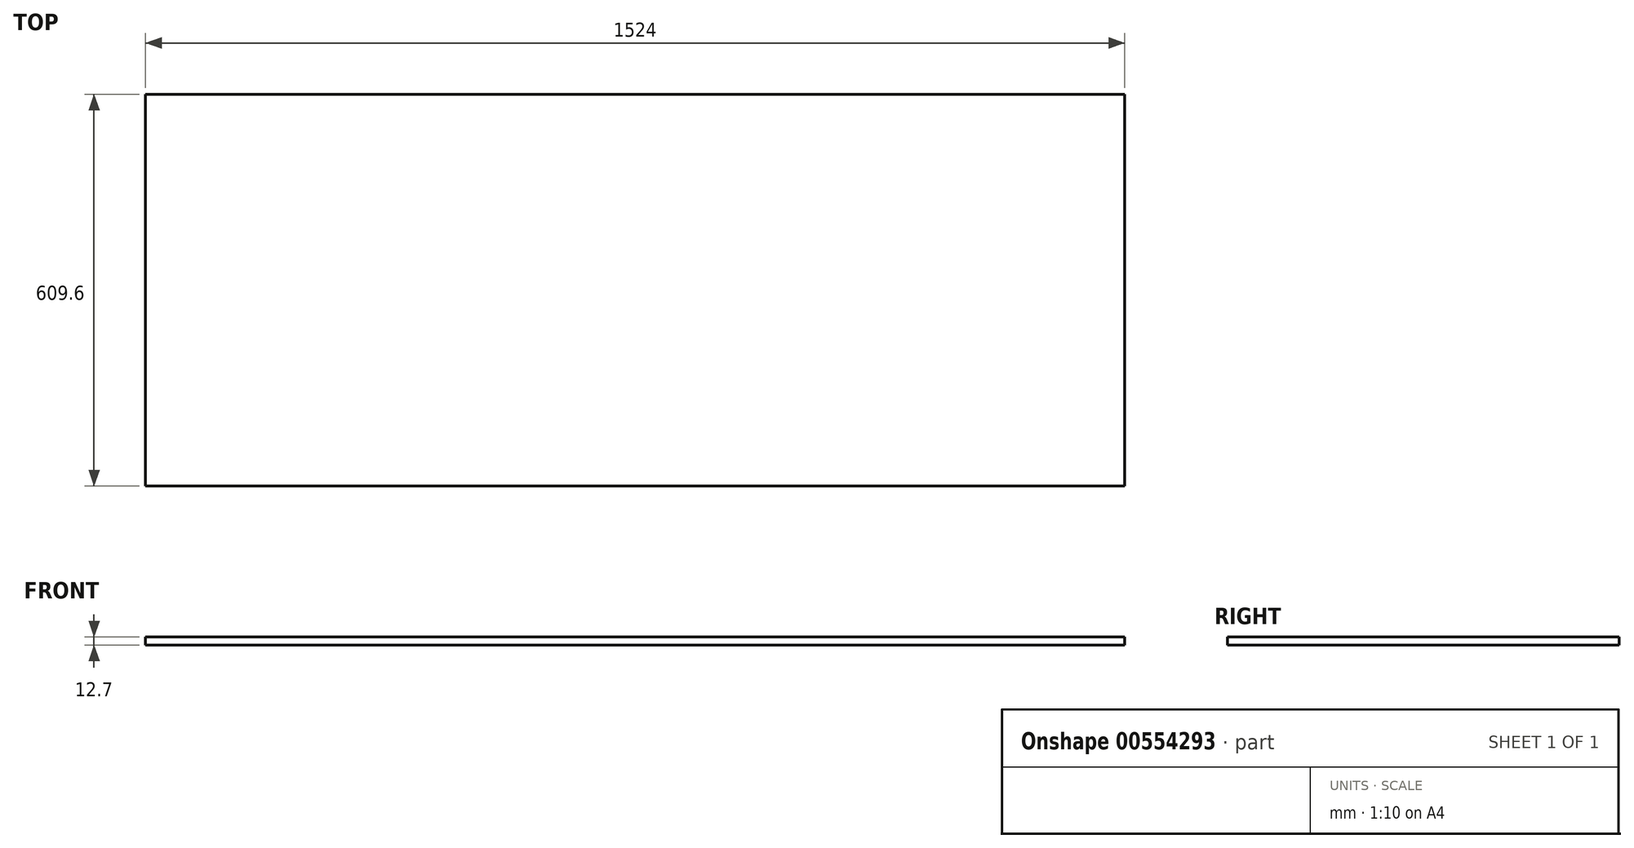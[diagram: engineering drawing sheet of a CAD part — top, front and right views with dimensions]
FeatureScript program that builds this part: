
annotation { "Feature Type Name" : "Feature", "Feature Type Description" : "" }
export const myFeature = defineFeature(function(context is Context, id is Id, definition is map)
    precondition{}
    {
        {
            var Q0;
            Q0=qCreatedBy(makeId("Top.planeOp"),FACE);
            var sketch = newSketch(context, id + "F0", { "sketchPlane" : qUnion([Q0])});
            skLineSegment(sketch, "E0.bottom", {"start": v(-584.49, 300.13) * mm, "end": v(939.51, 300.13) * mm});
            skLineSegment(sketch, "E0.top", {"start": v(-584.49, -309.47) * mm, "end": v(939.51, -309.47) * mm});
            skLineSegment(sketch, "E0.left", {"start": v(-584.49, 300.13) * mm, "end": v(-584.49, -309.47) * mm});
            skLineSegment(sketch, "E0.right", {"start": v(939.51, 300.13) * mm, "end": v(939.51, -309.47) * mm});
            skSolve(sketch);
        }
        {
            var Q0;
            Q0 = qSketchRegion(id + "F0", true);
            extrude(context, id + "F1", {"entities" : qUnion([Q0]), "depth" : 12.7 * mm, "offsetDistance" : 30.48 * mm});
        }
    });
